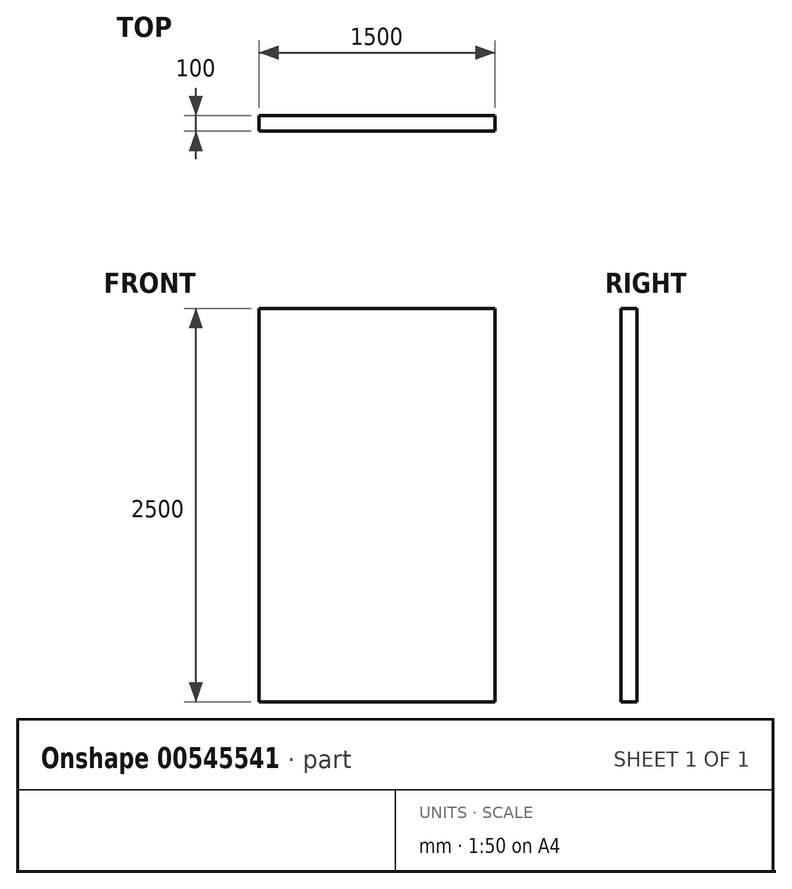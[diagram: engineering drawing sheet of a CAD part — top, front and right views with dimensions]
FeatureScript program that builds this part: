
annotation { "Feature Type Name" : "Feature", "Feature Type Description" : "" }
export const myFeature = defineFeature(function(context is Context, id is Id, definition is map)
    precondition{}
    {
        {
            var Q0;
            Q0=qCreatedBy(makeId("Front.planeOp"),FACE);
            var sketch = newSketch(context, id + "F0", { "sketchPlane" : qUnion([Q0])});
            skLineSegment(sketch, "E0.bottom", {"start": v(0, 0) * mm, "end": v(-1500, 0) * mm});
            skLineSegment(sketch, "E0.top", {"start": v(0, 2500) * mm, "end": v(-1500, 2500) * mm});
            skLineSegment(sketch, "E0.left", {"start": v(0, 0) * mm, "end": v(0, 2500) * mm});
            skLineSegment(sketch, "E0.right", {"start": v(-1500, 0) * mm, "end": v(-1500, 2500) * mm});
            skSolve(sketch);
        }
        {
            var Q0;
            Q0 = qSketchRegion(id + "F0", true);
            extrude(context, id + "F1", {"entities" : qUnion([Q0]), "depth" : 100 * mm, "offsetDistance" : 25 * mm});
        }
    });
